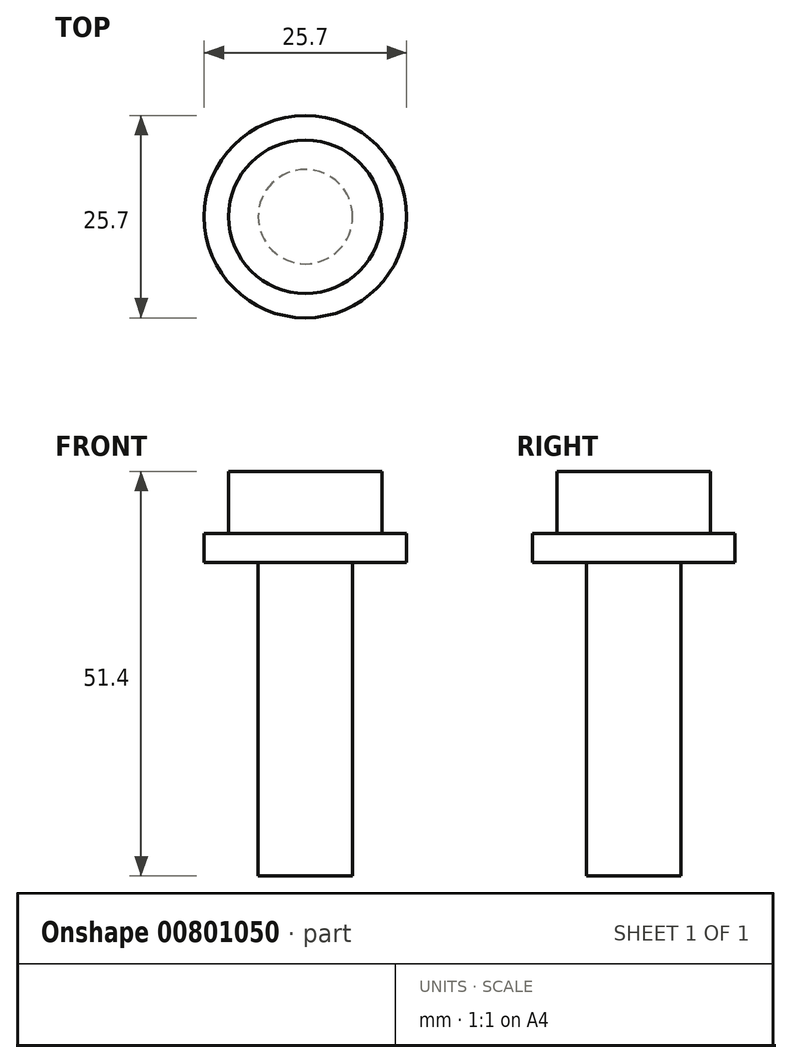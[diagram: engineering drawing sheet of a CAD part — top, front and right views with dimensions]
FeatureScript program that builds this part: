
annotation { "Feature Type Name" : "Feature", "Feature Type Description" : "" }
export const myFeature = defineFeature(function(context is Context, id is Id, definition is map)
    precondition{}
    {
        {
            var Q0;
            Q0=qCreatedBy(makeId("Front.planeOp"),FACE);
            var sketch = newSketch(context, id + "F0", { "sketchPlane" : qUnion([Q0])});
            skLineSegment(sketch, "E0", {"start": v(0, 0) * mm, "end": v(0, -51.4) * mm});
            skLineSegment(sketch, "E1", {"start": v(0, -51.4) * mm, "end": v(6, -51.4) * mm});
            skLineSegment(sketch, "E2", {"start": v(6, -51.4) * mm, "end": v(6, -11.6) * mm});
            skLineSegment(sketch, "E3", {"start": v(6, -11.6) * mm, "end": v(12.85, -11.6) * mm});
            skLineSegment(sketch, "E4", {"start": v(12.85, -11.6) * mm, "end": v(12.85, -7.9) * mm});
            skLineSegment(sketch, "E5", {"start": v(12.85, -7.9) * mm, "end": v(9.75, -7.9) * mm});
            skLineSegment(sketch, "E6", {"start": v(9.75, -7.9) * mm, "end": v(9.75, 0) * mm});
            skLineSegment(sketch, "E7", {"start": v(9.75, 0) * mm, "end": v(0, 0) * mm});
            skSolve(sketch);
        }
        {
            var Q0;
            Q0=makeQuery(id+"F0.imprint","IMPRINT",FACE,{"disambiguationData":[TD([[makeQuery(id+"F0.imprint","IMPRINT",EDGE,{"derivedFrom":sQuery(id+"F0.wireOp",EDGE,"E0")}),1.0]])]});
            var Q1;
            Q1=sQuery(id+"F0.wireOp",EDGE,"E0");
            revolve(context, id + "F1", {"surfaceOperationType" : NewSurfaceOperationType.NEW, "entities" : qUnion([Q0]), "axis" : qUnion([Q1]), "revolveType" : RevolveType.FULL});
        }
    });
